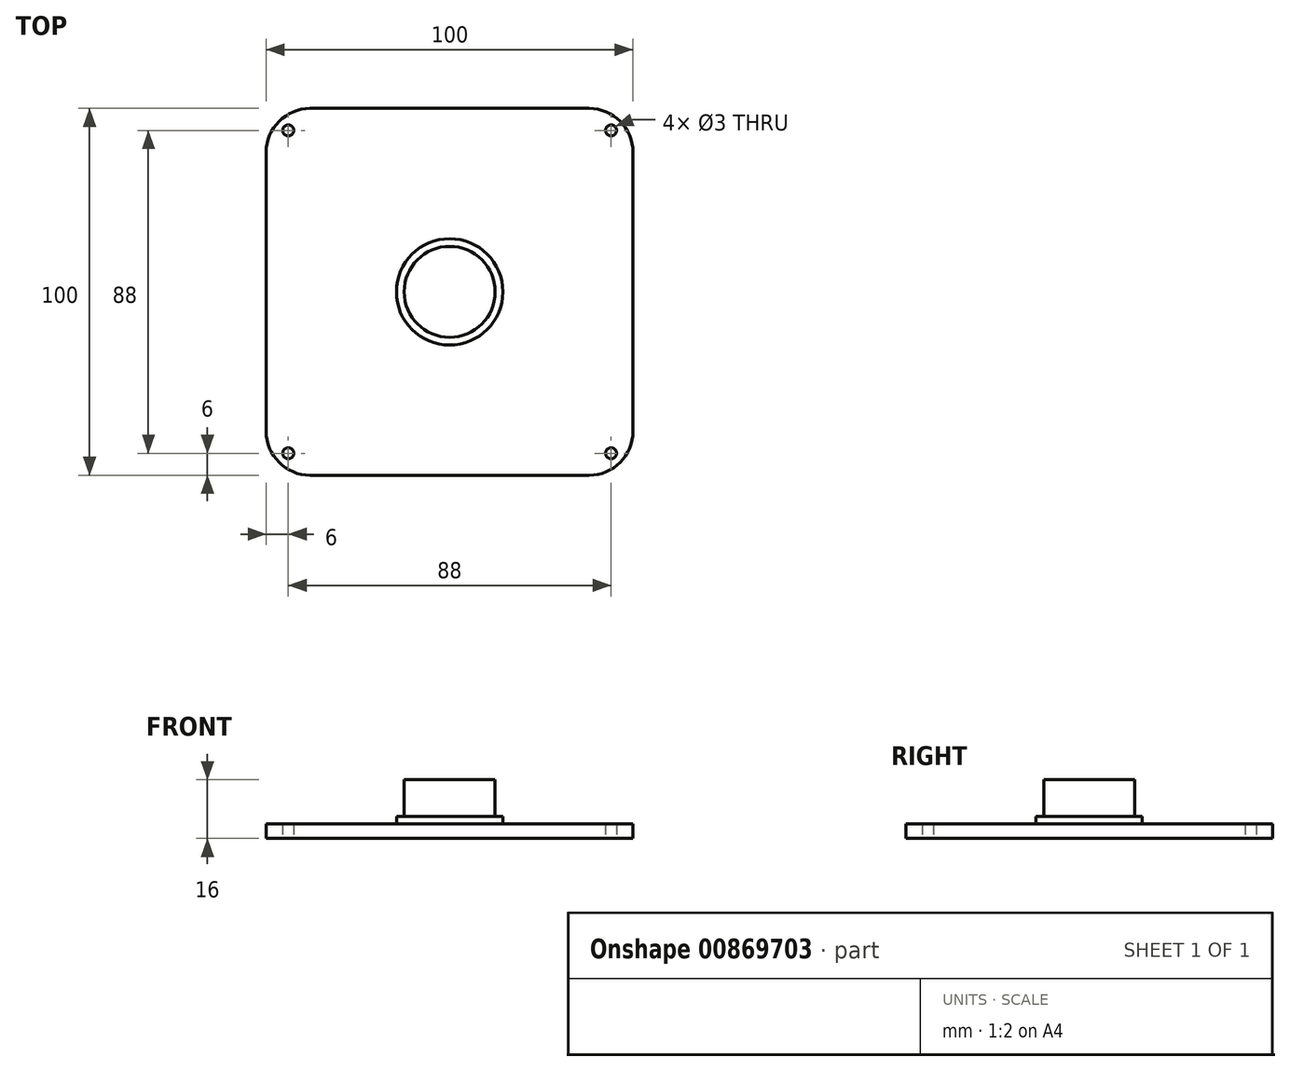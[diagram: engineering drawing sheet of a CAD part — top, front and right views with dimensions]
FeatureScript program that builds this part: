
annotation { "Feature Type Name" : "Feature", "Feature Type Description" : "" }
export const myFeature = defineFeature(function(context is Context, id is Id, definition is map)
    precondition{}
    {
        {
            var Q0;
            Q0=qCreatedBy(makeId("Top.planeOp"),FACE);
            var sketch = newSketch(context, id + "F0", { "sketchPlane" : qUnion([Q0])});
            skLineSegment(sketch, "E0.bottom", {"start": v(50, -50) * mm, "end": v(-50, -50) * mm});
            skLineSegment(sketch, "E0.top", {"start": v(50, 50) * mm, "end": v(-50, 50) * mm});
            skLineSegment(sketch, "E0.left", {"start": v(50, -50) * mm, "end": v(50, 50) * mm});
            skLineSegment(sketch, "E0.right", {"start": v(-50, -50) * mm, "end": v(-50, 50) * mm});
            skPoint(sketch, "E0.middle", {"position": v(0, 0) * mm});
            skLineSegment(sketch, "E1.bottom", {"start": v(47, -47) * mm, "end": v(-47, -47) * mm});
            skLineSegment(sketch, "E1.top", {"start": v(47, 47) * mm, "end": v(-47, 47) * mm});
            skLineSegment(sketch, "E1.left", {"start": v(47, -47) * mm, "end": v(47, 47) * mm});
            skLineSegment(sketch, "E1.right", {"start": v(-47, -47) * mm, "end": v(-47, 47) * mm});
            skLineSegment(sketch, "E2.bottom", {"start": v(-47, 47) * mm, "end": v(-44, 47) * mm, "construction": true});
            skLineSegment(sketch, "E2.top", {"start": v(-47, 44) * mm, "end": v(-44, 44) * mm, "construction": true});
            skLineSegment(sketch, "E2.left", {"start": v(-47, 47) * mm, "end": v(-47, 44) * mm, "construction": true});
            skLineSegment(sketch, "E2.right", {"start": v(-44, 47) * mm, "end": v(-44, 44) * mm, "construction": true});
            skLineSegment(sketch, "E3.bottom", {"start": v(47, 47) * mm, "end": v(44, 47) * mm, "construction": true});
            skLineSegment(sketch, "E3.top", {"start": v(47, 44) * mm, "end": v(44, 44) * mm, "construction": true});
            skLineSegment(sketch, "E3.left", {"start": v(47, 47) * mm, "end": v(47, 44) * mm, "construction": true});
            skLineSegment(sketch, "E3.right", {"start": v(44, 47) * mm, "end": v(44, 44) * mm, "construction": true});
            skLineSegment(sketch, "E4.bottom", {"start": v(47, -47) * mm, "end": v(44, -47) * mm, "construction": true});
            skLineSegment(sketch, "E4.top", {"start": v(47, -44) * mm, "end": v(44, -44) * mm, "construction": true});
            skLineSegment(sketch, "E4.left", {"start": v(47, -47) * mm, "end": v(47, -44) * mm, "construction": true});
            skLineSegment(sketch, "E4.right", {"start": v(44, -47) * mm, "end": v(44, -44) * mm, "construction": true});
            skLineSegment(sketch, "E5.bottom", {"start": v(-47, -47) * mm, "end": v(-44, -47) * mm, "construction": true});
            skLineSegment(sketch, "E5.top", {"start": v(-47, -44) * mm, "end": v(-44, -44) * mm, "construction": true});
            skLineSegment(sketch, "E5.left", {"start": v(-47, -47) * mm, "end": v(-47, -44) * mm, "construction": true});
            skLineSegment(sketch, "E5.right", {"start": v(-44, -47) * mm, "end": v(-44, -44) * mm, "construction": true});
            skCircle(sketch, "E6", {"center": v(-44, -44) * mm, "radius": 1.5 * mm});
            skCircle(sketch, "E7", {"center": v(-44, 44) * mm, "radius": 1.5 * mm});
            skCircle(sketch, "E8", {"center": v(44, 44) * mm, "radius": 1.5 * mm});
            skCircle(sketch, "E9", {"center": v(44, -44) * mm, "radius": 1.5 * mm});
            skCircle(sketch, "E10", {"center": v(-47, 47) * mm, "radius": 7.5 * mm});
            skCircle(sketch, "E11", {"center": v(47, 47) * mm, "radius": 7.5 * mm});
            skCircle(sketch, "E12", {"center": v(47, -47) * mm, "radius": 7.5 * mm});
            skCircle(sketch, "E13", {"center": v(-47, -47) * mm, "radius": 7.5 * mm});
            skCircle(sketch, "E14", {"center": v(0, 0) * mm, "radius": 14.5 * mm});
            skCircle(sketch, "E15", {"center": v(0, 0) * mm, "radius": 12.4 * mm});
            skSolve(sketch);
        }
        {
            var Q0;
            {var subQ0=sQuery(id+"F0.wireOp",EDGE,"E13");var subQ1=sQuery(id+"F0.wireOp",EDGE,"E0.right");var subQ2=makeQuery(id+"F0.imprint","INTERSECT",VERTEX,{"derivedFrom":[subQ1,subQ0]});Q0=makeQuery(id+"F0.imprint","IMPRINT",FACE,{"disambiguationData":[TD([[makeQuery(id+"F0.imprint","IMPRINT",EDGE,{"disambiguationData":[TD([[subQ2,-1.0]])],"derivedFrom":subQ1}),-1.0]])]});}
            var Q1;
            {var subQ5=sQuery(id+"F0.wireOp",EDGE,"E0.bottom");var subQ8=sQuery(id+"F0.wireOp",EDGE,"E0.right");var subQ9=makeQuery(id+"F0.imprint","INTERSECT",VERTEX,{"derivedFrom":[subQ5,subQ8]});Q1=makeQuery(id+"F0.imprint","IMPRINT",FACE,{"disambiguationData":[TD([[makeQuery(id+"F0.imprint","IMPRINT",EDGE,{"disambiguationData":[TD([[subQ9,1.0]])],"derivedFrom":subQ5}),-1.0]])]});}
            var Q2;
            Q2=makeQuery(id+"F0.imprint","IMPRINT",FACE,{"disambiguationData":[TD([[makeQuery(id+"F0.imprint","IMPRINT",EDGE,{"derivedFrom":sQuery(id+"F0.wireOp",EDGE,"E6")}),-1.0]])]});
            var Q3;
            {var subQ0=sQuery(id+"F0.wireOp",EDGE,"E12");var subQ1=sQuery(id+"F0.wireOp",EDGE,"E0.bottom");var subQ2=makeQuery(id+"F0.imprint","INTERSECT",VERTEX,{"derivedFrom":[subQ1,subQ0]});Q3=makeQuery(id+"F0.imprint","IMPRINT",FACE,{"disambiguationData":[TD([[makeQuery(id+"F0.imprint","IMPRINT",EDGE,{"disambiguationData":[TD([[subQ2,-1.0]])],"derivedFrom":subQ1}),-1.0]])]});}
            var Q4;
            {var subQ6=sQuery(id+"F0.wireOp",EDGE,"E0.left");var subQ7=sQuery(id+"F0.wireOp",EDGE,"E0.bottom");var subQ8=makeQuery(id+"F0.imprint","INTERSECT",VERTEX,{"derivedFrom":[subQ7,subQ6]});Q4=makeQuery(id+"F0.imprint","IMPRINT",FACE,{"disambiguationData":[TD([[makeQuery(id+"F0.imprint","IMPRINT",EDGE,{"disambiguationData":[TD([[subQ8,-1.0]])],"derivedFrom":subQ7}),-1.0]])]});}
            var Q5;
            Q5=makeQuery(id+"F0.imprint","IMPRINT",FACE,{"disambiguationData":[TD([[makeQuery(id+"F0.imprint","IMPRINT",EDGE,{"derivedFrom":sQuery(id+"F0.wireOp",EDGE,"E9")}),-1.0]])]});
            var Q6;
            {var subQ0=sQuery(id+"F0.wireOp",EDGE,"E12");var subQ1=sQuery(id+"F0.wireOp",EDGE,"E0.left");var subQ2=makeQuery(id+"F0.imprint","INTERSECT",VERTEX,{"derivedFrom":[subQ1,subQ0]});Q6=makeQuery(id+"F0.imprint","IMPRINT",FACE,{"disambiguationData":[TD([[makeQuery(id+"F0.imprint","IMPRINT",EDGE,{"disambiguationData":[TD([[subQ2,-1.0]])],"derivedFrom":subQ1}),1.0]])]});}
            var Q7;
            {var subQ6=sQuery(id+"F0.wireOp",EDGE,"E0.left");var subQ7=sQuery(id+"F0.wireOp",EDGE,"E0.top");var subQ8=makeQuery(id+"F0.imprint","INTERSECT",VERTEX,{"derivedFrom":[subQ7,subQ6]});Q7=makeQuery(id+"F0.imprint","IMPRINT",FACE,{"disambiguationData":[TD([[makeQuery(id+"F0.imprint","IMPRINT",EDGE,{"disambiguationData":[TD([[subQ8,-1.0]])],"derivedFrom":subQ7}),1.0]])]});}
            var Q8;
            Q8=makeQuery(id+"F0.imprint","IMPRINT",FACE,{"disambiguationData":[TD([[makeQuery(id+"F0.imprint","IMPRINT",EDGE,{"derivedFrom":sQuery(id+"F0.wireOp",EDGE,"E8")}),-1.0]])]});
            var Q9;
            {var subQ0=sQuery(id+"F0.wireOp",EDGE,"E11");var subQ1=sQuery(id+"F0.wireOp",EDGE,"E0.top");var subQ2=makeQuery(id+"F0.imprint","INTERSECT",VERTEX,{"derivedFrom":[subQ1,subQ0]});Q9=makeQuery(id+"F0.imprint","IMPRINT",FACE,{"disambiguationData":[TD([[makeQuery(id+"F0.imprint","IMPRINT",EDGE,{"disambiguationData":[TD([[subQ2,-1.0]])],"derivedFrom":subQ1}),1.0]])]});}
            var Q10;
            {var subQ6=sQuery(id+"F0.wireOp",EDGE,"E0.top");var subQ8=sQuery(id+"F0.wireOp",EDGE,"E0.right");var subQ9=makeQuery(id+"F0.imprint","INTERSECT",VERTEX,{"derivedFrom":[subQ6,subQ8]});Q10=makeQuery(id+"F0.imprint","IMPRINT",FACE,{"disambiguationData":[TD([[makeQuery(id+"F0.imprint","IMPRINT",EDGE,{"disambiguationData":[TD([[subQ9,1.0]])],"derivedFrom":subQ6}),1.0]])]});}
            var Q11;
            Q11=makeQuery(id+"F0.imprint","IMPRINT",FACE,{"disambiguationData":[TD([[makeQuery(id+"F0.imprint","IMPRINT",EDGE,{"derivedFrom":sQuery(id+"F0.wireOp",EDGE,"E7")}),-1.0]])]});
            var Q12;
            {var subQ10=sQuery(id+"F0.wireOp",EDGE,"E12");var subQ13=sQuery(id+"F0.wireOp",EDGE,"E1.bottom");var subQ14=makeQuery(id+"F0.imprint","INTERSECT",VERTEX,{"derivedFrom":[subQ13,subQ10]});Q12=makeQuery(id+"F0.imprint","IMPRINT",FACE,{"disambiguationData":[TD([[makeQuery(id+"F0.imprint","IMPRINT",EDGE,{"disambiguationData":[TD([[subQ14,-1.0]])],"derivedFrom":subQ13}),-1.0]])]});}
            extrude(context, id + "F1", {"entities" : qUnion([Q0, Q1, Q2, Q3, Q4, Q5, Q6, Q7, Q8, Q9, Q10, Q11, Q12]), "depth" : 4 * mm, "offsetDistance" : 25 * mm});
        }
        {
            var Q0;
            Q0=makeQuery(id+"F1.opExtrude","SWEPT_EDGE",EDGE,{"disambiguationData":[OSD([sQuery(id+"F0.wireOp",EDGE,"E0.top"),sQuery(id+"F0.wireOp",EDGE,"E0.right")])]});
            var Q1;
            Q1=makeQuery(id+"F1.opExtrude","SWEPT_EDGE",EDGE,{"disambiguationData":[OSD([sQuery(id+"F0.wireOp",EDGE,"E0.top"),sQuery(id+"F0.wireOp",EDGE,"E0.left")])]});
            var Q2;
            Q2=makeQuery(id+"F1.opExtrude","SWEPT_EDGE",EDGE,{"disambiguationData":[OSD([sQuery(id+"F0.wireOp",EDGE,"E0.bottom"),sQuery(id+"F0.wireOp",EDGE,"E0.left")])]});
            var Q3;
            Q3=makeQuery(id+"F1.opExtrude","SWEPT_EDGE",EDGE,{"disambiguationData":[OSD([sQuery(id+"F0.wireOp",EDGE,"E0.bottom"),sQuery(id+"F0.wireOp",EDGE,"E0.right")])]});
            fillet(context, id + "F2", {"entities" : qUnion([Q0, Q1, Q2, Q3]), "radius" : 12 * mm, "tangentPropagation" : true, "allowEdgeOverflow" : false});
        }
        {
            var Q0;
            Q0=makeQuery(id+"F0.imprint","IMPRINT",FACE,{"disambiguationData":[TD([[makeQuery(id+"F0.imprint","IMPRINT",EDGE,{"derivedFrom":sQuery(id+"F0.wireOp",EDGE,"E14")}),1.0]])]});
            extrude(context, id + "F3", {"entities" : qUnion([Q0]), "operationType" : NewBodyOperationType.ADD, "depth" : 6 * mm, "offsetDistance" : 25 * mm});
        }
        {
            var Q0;
            Q0=makeQuery(id+"F0.imprint","IMPRINT",FACE,{"disambiguationData":[TD([[makeQuery(id+"F0.imprint","IMPRINT",EDGE,{"derivedFrom":sQuery(id+"F0.wireOp",EDGE,"E15")}),1.0]])]});
            extrude(context, id + "F4", {"entities" : qUnion([Q0]), "operationType" : NewBodyOperationType.ADD, "depth" : 16 * mm, "offsetDistance" : 25 * mm});
        }
    });
